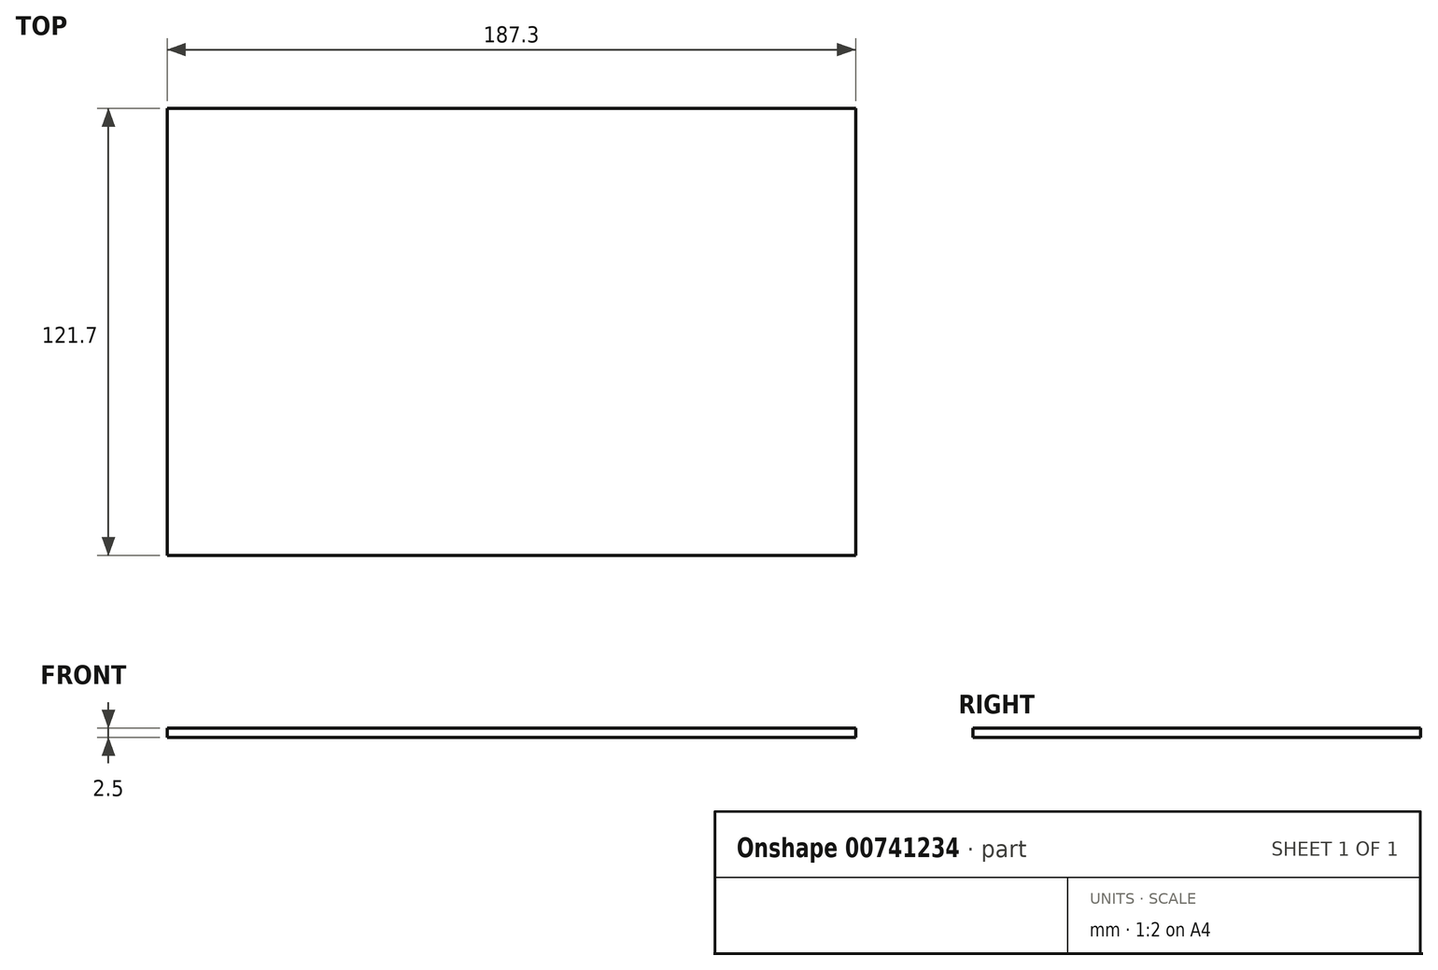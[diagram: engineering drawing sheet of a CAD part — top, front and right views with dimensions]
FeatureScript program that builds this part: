
annotation { "Feature Type Name" : "Feature", "Feature Type Description" : "" }
export const myFeature = defineFeature(function(context is Context, id is Id, definition is map)
    precondition{}
    {
        {
            var Q0;
            Q0=qCreatedBy(makeId("Top.planeOp"),FACE);
            var sketch = newSketch(context, id + "F0", { "sketchPlane" : qUnion([Q0])});
            skLineSegment(sketch, "E0.bottom", {"start": v(0, 0) * mm, "end": v(187.3, 0) * mm});
            skLineSegment(sketch, "E0.top", {"start": v(0, 121.7) * mm, "end": v(187.3, 121.7) * mm});
            skLineSegment(sketch, "E0.left", {"start": v(0, 0) * mm, "end": v(0, 121.7) * mm});
            skLineSegment(sketch, "E0.right", {"start": v(187.3, 0) * mm, "end": v(187.3, 121.7) * mm});
            skSolve(sketch);
        }
        {
            var Q0;
            Q0=makeQuery(id+"F0.imprint","IMPRINT",FACE,{"disambiguationData":[TD([[makeQuery(id+"F0.imprint","IMPRINT",EDGE,{"derivedFrom":sQuery(id+"F0.wireOp",EDGE,"E0.bottom")}),1.0]])]});
            extrude(context, id + "F1", {"entities" : qUnion([Q0]), "depth" : 2.5 * mm, "offsetDistance" : 25 * mm});
        }
    });
